# Revit family: Bath-Freestanding-BubbleMassage-Air_Bath-Heated_Surface-KOHLER-Stargaze
name_source: partatom
category: Plumbing Fixtures
revit_build: Autodesk Revit 2015 (Build: 20140606_1530(x64)
units: mm (PartAtom-declared; Revit-internal decimal feet)

## types (2) — shared parameters
ADA Compliant = No
Amplifier Electrical Connector = Amplifier Electrical Connector
Apparent Load = 1800 VA
Assembly Code = D2010500
Blower Electrical Connector = Blower Electrical Connector
CW Connection = No
Cold Water Inlet = Cold Water Inlet
Date Modified = 10/25/2018
Default Elevation = 0"
Description = 72 inch x 36 inch freestanding BubbleMassage Air Bath with Bask  heated surface and fluted shroud
Drain Included = No
Electrical Connector = Yes
Electrical Note = One circuit required, protected with Class A Ground-Fault
Circuit-Interrupter (GFCI) or Residual Current Device (RCD)
HW Connection = No
Heater Electrical Connector = Heater Electrical Connector
Height = 25"
Hot Water Inlet = Hot Water Inlet
Length = 72"
Manufacturer = KOHLER Co.
MasterFormat 1995 = 15410
MasterFormat 2004 = 22.41.19
Material = Acrylic
Product Documentation Link = http://www.us.kohler.com
Product Name = Stargaze
Product Page URL = http://www.us.kohler.com
Pump Electrical Connector = Pump Electrical Connector
URL = https://www.us.kohler.com
Vent Connection = No
Voltage = 120 V
Waste Connection = Yes
Waste Water Outlet = Waste Water Outlet
Width = 36 1/16"

## per-type parameters (varying)
| type | Finish | Model | Type |
| 0-White | Kohler-Acrylic-0-White | K-1959-GW-0 | 1 |
| 96-Biscuit | Kohler-Acrylic-96-Biscuit | K-1959-GW-96 | 2 |

## geometry (parser evidence)
native form markers: Sweep x4
no freeform markers — native parametric forms only
